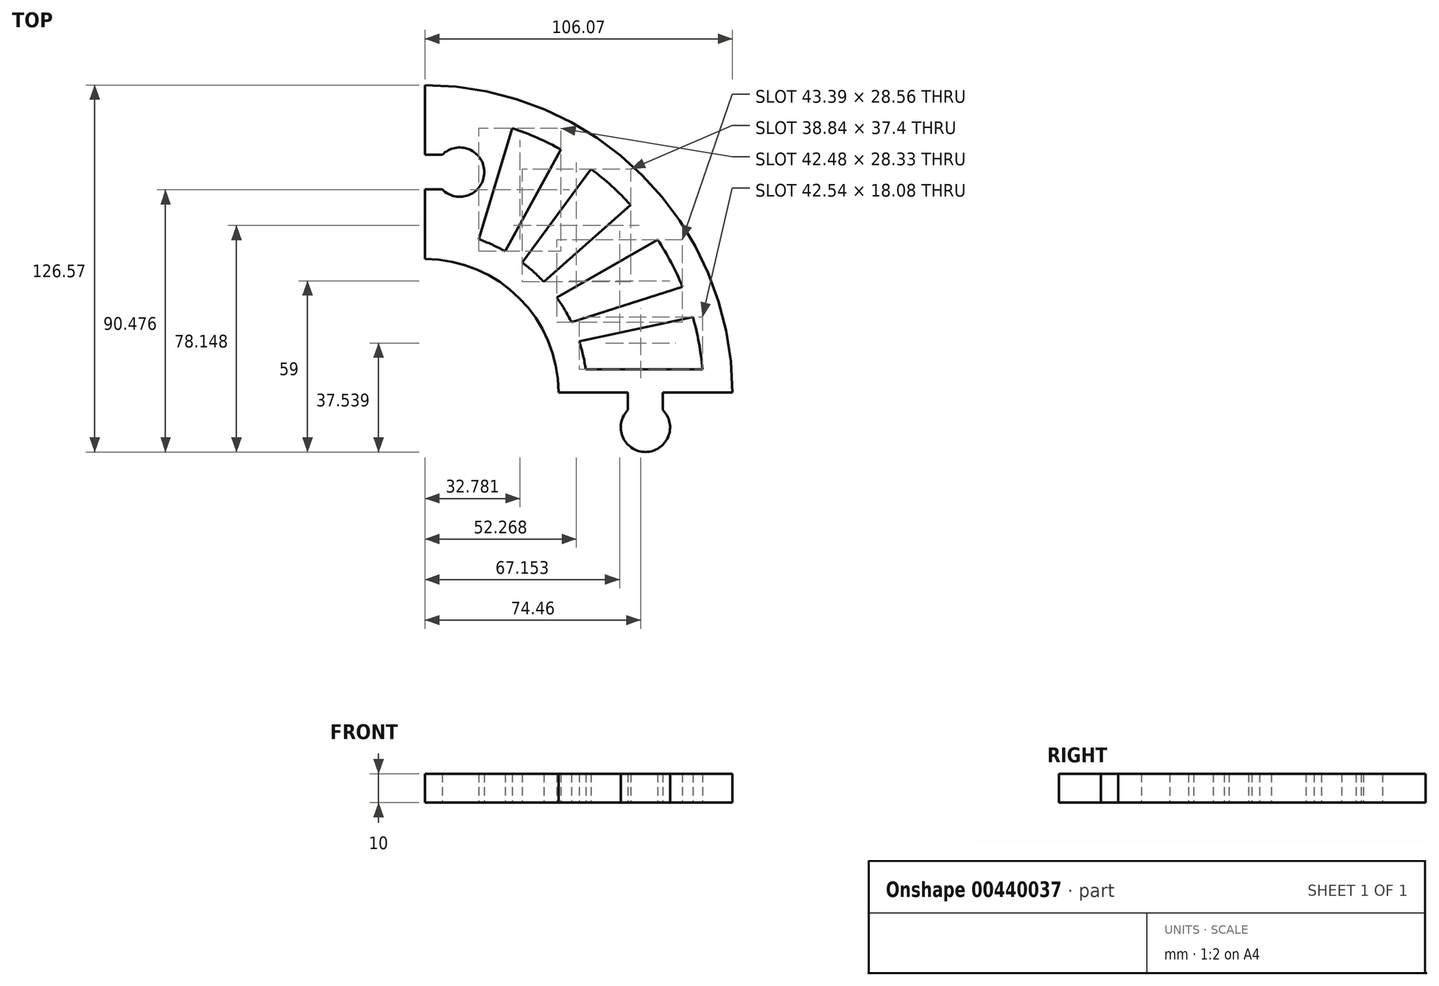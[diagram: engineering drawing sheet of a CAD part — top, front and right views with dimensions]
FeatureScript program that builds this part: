
annotation { "Feature Type Name" : "Feature", "Feature Type Description" : "" }
export const myFeature = defineFeature(function(context is Context, id is Id, definition is map)
    precondition{}
    {
        {
            var Q0;
            Q0=qCreatedBy(makeId("Top.planeOp"),FACE);
            var sketch = newSketch(context, id + "F0", { "sketchPlane" : qUnion([Q0])});
            skArc(sketch, "E0", {"start": v(106.07, 0) * mm, "mid": v(75, 75) * mm, "end": v(0, 106.07) * mm});
            skArc(sketch, "E1", {"start": v(46.07, 0) * mm, "mid": v(32.57, 32.57) * mm, "end": v(0, 46.07) * mm});
            skLineSegment(sketch, "E2", {"start": v(0, 106.07) * mm, "end": v(0, 82.07) * mm});
            skLineSegment(sketch, "E3", {"start": v(46.07, 0) * mm, "end": v(106.07, 0) * mm});
            skArc(sketch, "E4", {"start": v(70.07, -5.98) * mm, "mid": v(76.07, -20.5) * mm, "end": v(82.07, -5.98) * mm});
            skLineSegment(sketch, "E5", {"start": v(70.07, -5.98) * mm, "end": v(70.07, 0) * mm});
            skLineSegment(sketch, "E6", {"start": v(82.07, 0) * mm, "end": v(82.07, -5.98) * mm});
            skArc(sketch, "E7", {"start": v(5.98, 70.07) * mm, "mid": v(20.5, 76.07) * mm, "end": v(5.98, 82.07) * mm});
            skPoint(sketch, "E8.startSnap0", {"position": v(0, 82.07) * mm});
            skLineSegment(sketch, "E9", {"start": v(5.98, 70.07) * mm, "end": v(0, 70.07) * mm});
            skLineSegment(sketch, "E10", {"start": v(0, 82.07) * mm, "end": v(5.98, 82.07) * mm});
            skPoint(sketch, "E8.end.orphan", {"position": v(0, 76.07) * mm});
            skLineSegment(sketch, "E11.trimOffspring", {"start": v(0, 70.07) * mm, "end": v(0, 46.07) * mm});
            skArc(sketch, "E12", {"start": v(95.73, 8) * mm, "mid": v(94.53, 17.12) * mm, "end": v(92.46, 26.08) * mm});
            skArc(sketch, "E13", {"start": v(55.5, 8) * mm, "mid": v(54.56, 12.92) * mm, "end": v(53.19, 17.73) * mm});
            skLineSegment(sketch, "E14", {"start": v(56.07, 0) * mm, "end": v(96.07, 0) * mm});
            skLineSegment(sketch, "E15", {"start": v(55.5, 8) * mm, "end": v(95.73, 8) * mm});
            skLineSegment(sketch, "E16", {"start": v(53.19, 17.73) * mm, "end": v(92.46, 26.08) * mm});
            skLineSegment(sketch, "E17", {"start": v(50.56, 24.22) * mm, "end": v(88.85, 36.53) * mm});
            skLineSegment(sketch, "E18", {"start": v(45.46, 32.82) * mm, "end": v(80.27, 52.78) * mm});
            skLineSegment(sketch, "E19", {"start": v(41.01, 38.23) * mm, "end": v(70.97, 64.75) * mm});
            skLineSegment(sketch, "E20", {"start": v(33.57, 44.9) * mm, "end": v(57.35, 77.07) * mm});
            skLineSegment(sketch, "E21", {"start": v(27.71, 48.74) * mm, "end": v(46.95, 83.81) * mm});
            skLineSegment(sketch, "E22", {"start": v(18.61, 52.89) * mm, "end": v(30.14, 91.21) * mm});
            skArc(sketch, "E23.trimOffspring", {"start": v(46.95, 83.81) * mm, "mid": v(38.72, 87.92) * mm, "end": v(30.14, 91.21) * mm});
            skArc(sketch, "E24.trimOffspring", {"start": v(27.71, 48.74) * mm, "mid": v(23.26, 51.02) * mm, "end": v(18.61, 52.89) * mm});
            skArc(sketch, "E25.trimOffspring", {"start": v(70.97, 64.75) * mm, "mid": v(64.45, 71.24) * mm, "end": v(57.35, 77.07) * mm});
            skArc(sketch, "E26.trimOffspring", {"start": v(41.01, 38.23) * mm, "mid": v(37.44, 41.73) * mm, "end": v(33.57, 44.9) * mm});
            skArc(sketch, "E27.trimOffspring", {"start": v(88.85, 36.53) * mm, "mid": v(84.95, 44.86) * mm, "end": v(80.27, 52.78) * mm});
            skArc(sketch, "E28.trimOffspring", {"start": v(50.56, 24.22) * mm, "mid": v(48.2, 28.63) * mm, "end": v(45.46, 32.82) * mm});
            skSolve(sketch);
        }
        {
            var Q0;
            Q0 = qSketchRegion(id + "F0", true);
            extrude(context, id + "F1", {"entities" : qUnion([Q0]), "depth" : 10 * mm});
        }
    });
